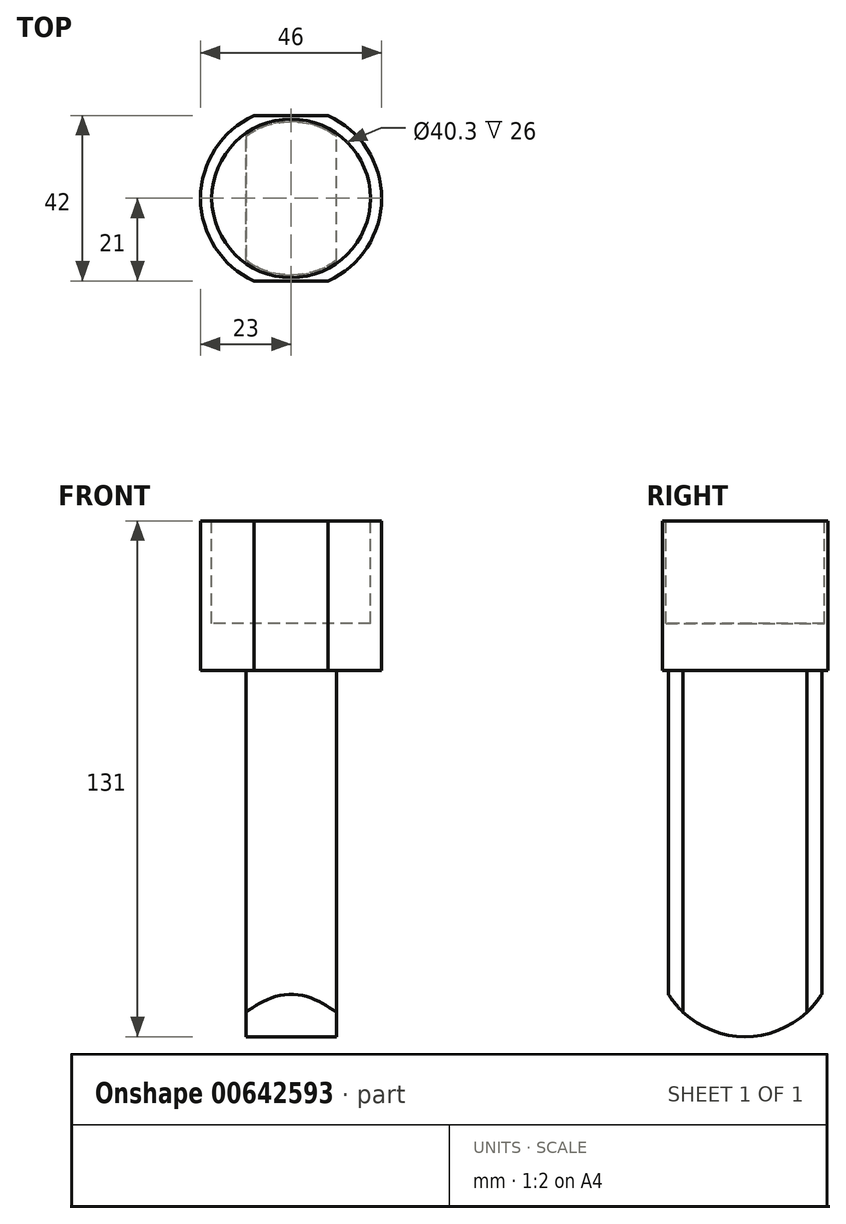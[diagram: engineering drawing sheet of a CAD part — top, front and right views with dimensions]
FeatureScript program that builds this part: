
annotation { "Feature Type Name" : "Feature", "Feature Type Description" : "" }
export const myFeature = defineFeature(function(context is Context, id is Id, definition is map)
    precondition{}
    {
        {
            var Q0;
            Q0=qCreatedBy(makeId("Top.planeOp"),FACE);
            var sketch = newSketch(context, id + "F0", { "sketchPlane" : qUnion([Q0])});
            skArc(sketch, "E0", {"start": v(-9.38, 21) * mm, "mid": v(-23, 0) * mm, "end": v(-9.38, -21) * mm});
            skLineSegment(sketch, "E1", {"start": v(9.38, 21) * mm, "end": v(-9.38, 21) * mm});
            skLineSegment(sketch, "E2.MirrorCS", {"start": v(9.38, -21) * mm, "end": v(-9.38, -21) * mm});
            skArc(sketch, "E3.trimOffspring", {"start": v(9.38, -21) * mm, "mid": v(23, 0) * mm, "end": v(9.38, 21) * mm});
            skSolve(sketch);
        }
        {
            var Q0;
            Q0 = qSketchRegion(id + "F0", true);
            extrude(context, id + "F1", {"entities" : qUnion([Q0]), "depth" : 38 * mm, "offsetDistance" : 25 * mm});
        }
        {
            var Q0;
            Q0=makeQuery(id+"F1.opExtrude","CAP_FACE",FACE,{"disambiguationData":[OSD([sQuery(id+"F0.wireOp",EDGE,"E0"),sQuery(id+"F0.wireOp",EDGE,"E1"),sQuery(id+"F0.wireOp",EDGE,"E2.MirrorCS"),sQuery(id+"F0.wireOp",EDGE,"E3.trimOffspring")])],"isStart":false});
            var sketch = newSketch(context, id + "F2", { "sketchPlane" : qUnion([Q0])});
            skCircle(sketch, "E4", {"center": v(0, 0) * mm, "radius": 20.15 * mm});
            skSolve(sketch);
        }
        {
            var Q0;
            Q0 = qSketchRegion(id + "F2", true);
            extrude(context, id + "F3", {"entities" : qUnion([Q0]), "operationType" : NewBodyOperationType.REMOVE, "oppositeDirection" : true, "depth" : 26 * mm, "offsetDistance" : 25 * mm});
        }
        {
            var Q0;
            Q0=makeQuery(id+"F1.opExtrude","CAP_FACE",FACE,{"disambiguationData":[OSD([sQuery(id+"F0.wireOp",EDGE,"E0"),sQuery(id+"F0.wireOp",EDGE,"E1"),sQuery(id+"F0.wireOp",EDGE,"E2.MirrorCS"),sQuery(id+"F0.wireOp",EDGE,"E3.trimOffspring")])],"isStart":true});
            var sketch = newSketch(context, id + "F4", { "sketchPlane" : qUnion([Q0])});
            skArc(sketch, "E5", {"start": v(-11.5, -15.75) * mm, "mid": v(0, -19.5) * mm, "end": v(11.5, -15.75) * mm});
            skLineSegment(sketch, "E6", {"start": v(-11.5, 15.75) * mm, "end": v(-11.5, -15.75) * mm});
            skLineSegment(sketch, "E7.MirrorCS", {"start": v(11.5, 15.75) * mm, "end": v(11.5, -15.75) * mm});
            skArc(sketch, "E8.trimOffspring", {"start": v(11.5, 15.75) * mm, "mid": v(0, 19.5) * mm, "end": v(-11.5, 15.75) * mm});
            skSolve(sketch);
        }
        {
            var Q0;
            Q0=makeQuery(id+"F4.imprint","IMPRINT",FACE,{"disambiguationData":[TD([[makeQuery(id+"F4.imprint","IMPRINT",EDGE,{"derivedFrom":sQuery(id+"F4.wireOp",EDGE,"E5")}),1.0]])]});
            extrude(context, id + "F5", {"entities" : qUnion([Q0]), "operationType" : NewBodyOperationType.ADD, "depth" : 93 * mm, "offsetDistance" : 25 * mm});
        }
        {
            var Q0;
            Q0=makeQuery(id+"F5.opExtrude","SWEPT_FACE",FACE,{"disambiguationData":[OSD([sQuery(id+"F4.wireOp",EDGE,"E6")])]});
            var sketch = newSketch(context, id + "F6", { "sketchPlane" : qUnion([Q0])});
            skCircle(sketch, "E9", {"center": v(0, -70) * mm, "radius": 23 * mm});
            skLineSegment(sketch, "E10", {"start": v(23, -69.67) * mm, "end": v(23, -108.39) * mm});
            skLineSegment(sketch, "E11", {"start": v(23, -108.39) * mm, "end": v(-35.86, -106) * mm});
            skLineSegment(sketch, "E12", {"start": v(-35.86, -106) * mm, "end": v(-22.98, -68.97) * mm});
            skSolve(sketch);
        }
        {
            var Q0;
            {var subQ0=sQuery(id+"F6.wireOp",EDGE,"E9");var subQ1=sQuery(id+"F4.wireOp",EDGE,"E6");var subQ4=makeQuery(id+"F5.opExtrude","CAP_EDGE",EDGE,{"disambiguationData":[OSD([subQ1])],"isStart":false});var subQ5=makeQuery(id+"F6.imprint","INTERSECT",VERTEX,{"derivedFrom":[subQ4,subQ0]});Q0=makeQuery(id+"F6.imprint","IMPRINT",FACE,{"disambiguationData":[TD([[makeQuery(id+"F6.imprint","IMPRINT",EDGE,{"disambiguationData":[TD([[subQ5,1.0]])],"derivedFrom":subQ0}),-1.0]])]});}
            var Q1;
            {var subQ0=sQuery(id+"F6.wireOp",EDGE,"E9");var subQ1=sQuery(id+"F4.wireOp",EDGE,"E6");var subQ2=makeQuery(id+"F5.opExtrude","CAP_EDGE",EDGE,{"disambiguationData":[OSD([subQ1])],"isStart":false});var subQ3=makeQuery(id+"F6.imprint","INTERSECT",VERTEX,{"derivedFrom":[subQ2,subQ0]});Q1=makeQuery(id+"F6.imprint","IMPRINT",FACE,{"disambiguationData":[TD([[makeQuery(id+"F6.imprint","IMPRINT",EDGE,{"disambiguationData":[TD([[subQ3,-1.0]])],"derivedFrom":subQ0}),-1.0]])]});}
            var Q2;
            {var subQ0=sQuery(id+"F6.wireOp",EDGE,"E11");Q2=makeQuery(id+"F6.imprint","IMPRINT",FACE,{"disambiguationData":[TD([[makeQuery(id+"F6.imprint","IMPRINT",EDGE,{"derivedFrom":subQ0}),-1.0]])]});}
            extrude(context, id + "F7", {"entities" : qUnion([Q0, Q1, Q2]), "operationType" : NewBodyOperationType.REMOVE, "endBound" : BoundingType.THROUGH_ALL, "oppositeDirection" : true, "depth" : 25 * mm, "offsetDistance" : 25 * mm});
        }
    });
